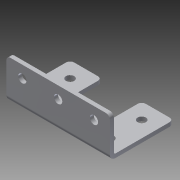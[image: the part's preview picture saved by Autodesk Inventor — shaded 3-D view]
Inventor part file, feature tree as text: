
AUTODESK INVENTOR PART (.ipt)
format: ipt  version: 2013 (Build 170138000, 138)  size: 232,448 bytes
history: native  units: in
note: dims shown in document units (in); Inventor stores cm internally (conversion verified against a paired STEP export)
features: sheet_metal_op x4, other x4, sketch x3, chamfer x1
ambient origin geometry x8: Origin, YZ Plane, XZ Plane, XY Plane, X Axis, Y Axis, Z Axis, Center Point
bodies: Solid1 (feature_tree)
feature tree (12):
  sheet_metal_op  "Face1"
  sheet_metal_op  "Flange1"
  chamfer  "Corner Round1"
  sketch  "Sketch1"  dims[d0=3.25in]
  other  "Plate1"
  sketch  "Sketch2"  dims[d2=0.5in]
  other  "Plate2"
  sheet_metal_op  "Bend1"
  sheet_metal_op  "Corner1"
  sketch  "Sketch3"  dims[d3=0.5in d4=0.26in d5=0.75in d6=0.75in d7=0.5in d8=1.0in d9=1.0in d10=0.5in d11=0.5in d12=1.0in d13=0.125in d14=0.125in d15=0.0625in d16=0.25in d17=0.125in d18=1.25in d19=90.0deg d20=0.05in d21=0.5in d22=0.125in d23=0.125in d24=0.26in d26=0.5in d27=0.875in d28=0.125in d29=0.0in d30=0.125in]
  other  "Cut1"
  other  "Definition1"
